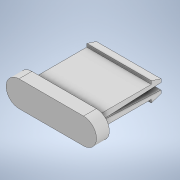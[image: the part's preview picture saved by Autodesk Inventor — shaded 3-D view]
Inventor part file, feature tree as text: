
AUTODESK INVENTOR PART (.ipt)
format: ipt  version: 2020.3 (Build 243373000, 373)  size: 131,584 bytes
history: native  units: mm
features: extrude x4, sketch x4
ambient origin geometry x8: Origin, YZ Plane, XZ Plane, XY Plane, X Axis, Y Axis, Z Axis, Center Point
bodies: Solid1 (feature_tree)
feature tree (8):
  extrude  "Extrusion1"  Depth=10.0mm TaperAngle=0.0deg
  extrude  "Extrusion2"  Depth=1.5mm
  extrude  "Extrusion3"  Depth=10.0mm TaperAngle=0.0deg
  extrude  "Extrusion4"  Depth=2.0mm
  sketch  "Sketch1"  dims[d3=2.0mm d4=0.0mm d6=10.0mm d7=0.0mm]
  sketch  "Sketch2"  dims[d8=1.5mm d9=0.5mm]
  sketch  "Sketch3"  dims[d10=0.5mm d11=10.0mm d12=0.0mm]
  sketch  "Sketch4"  dims[d13=0.5mm d14=0.5mm d15=2.0mm d16=0.0mm]
